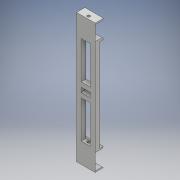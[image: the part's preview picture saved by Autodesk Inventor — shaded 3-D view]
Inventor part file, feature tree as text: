
AUTODESK INVENTOR PART (.ipt)
format: ipt  version: 2018 (Build 220112000, 112)  size: 431,616 bytes
history: native  units: mm
features: extrude x7, sketch x7, chamfer x5
ambient origin geometry x8: Origin, YZ Plane, XZ Plane, XY Plane, X Axis, Y Axis, Z Axis, Center Point
bodies: Solid1 (feature_tree)
feature tree (19):
  extrude  "Extrusion1"  Depth=140.0mm
  extrude  "Extrusion2"  Depth=20.0mm
  extrude  "Extrusion3"  Depth=4.0mm TaperAngle=0.0deg
  extrude  "Extrusion4"  Depth=10.0mm
  extrude  "Extrusion5"  Depth=10.0mm
  chamfer  "Chamfer1"  Distance=5.0mm
  chamfer  "Chamfer2"  Distance=50.0mm
  chamfer  "Chamfer3"  Distance=2.0mm
  extrude  "Extrusion8"  Depth=10.0mm
  extrude  "Extrusion9"  Depth=10.0mm
  chamfer  "Chamfer4"  Distance=5.0mm
  chamfer  "Chamfer5"  Distance=5.0mm
  sketch  "Sketch1"  dims[d0=20.0mm d1=140.0mm]
  sketch  "Sketch2"  dims[d2=5.0mm d3=0.0mm d4=20.0mm]
  sketch  "Sketch3"  dims[d5=20.0mm d6=4.0mm d7=0.0mm]
  sketch  "Sketch4"  dims[d8=5.0mm d9=10.0mm]
  sketch  "Sketch5"  dims[d10=5.0mm d11=10.0mm d12=5.0mm d13=0.0mm d15=50.0mm d16=0.0mm]
  sketch  "Sketch8"  dims[d17=2.0mm]
  sketch  "Sketch9"  dims[d18=5.0mm d19=2.0mm d21=5.0mm d22=2.5mm d23=5.0mm d24=5.0mm d25=5.0mm d26=10.0mm d27=0.0mm d28=4.0mm d29=2.0mm d30=45.0deg d31=5.0mm d32=2.0mm d33=45.0deg d34=3.5mm d35=2.0mm d36=45.0deg d46=2.0mm d53=3.0mm d54=3.0mm d55=30.0mm d56=0.0mm d57=5.0mm d58=30.0mm d59=0.0mm d60=2.0mm d61=3.0mm d62=2.0mm d63=45.0deg d64=3.0mm d65=2.0mm d66=45.0deg]
